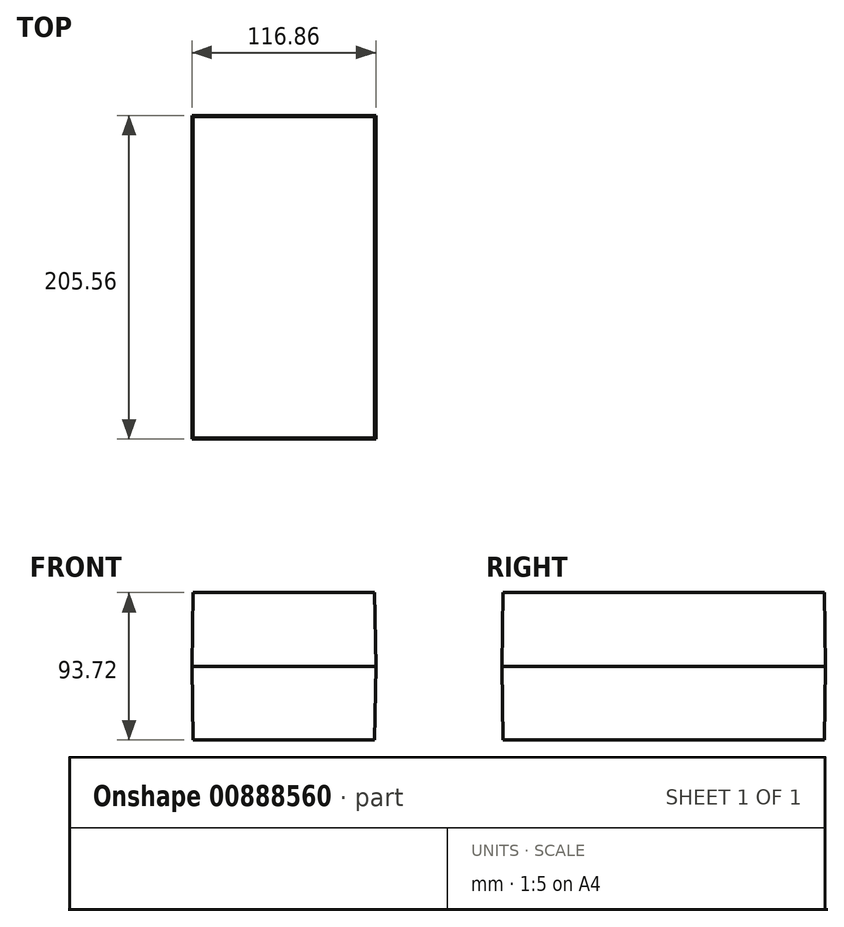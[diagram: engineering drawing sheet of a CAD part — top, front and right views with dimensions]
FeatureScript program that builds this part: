
annotation { "Feature Type Name" : "Feature", "Feature Type Description" : "" }
export const myFeature = defineFeature(function(context is Context, id is Id, definition is map)
    precondition{}
    {
        {
            var Q0;
            Q0=qCreatedBy(makeId("Top.planeOp"),FACE);
            var sketch = newSketch(context, id + "F0", { "sketchPlane" : qUnion([Q0])});
            skLineSegment(sketch, "E0.bottom", {"start": v(-103.11, 32.39) * mm, "end": v(13.75, 32.39) * mm});
            skLineSegment(sketch, "E0.top", {"start": v(-103.11, -173.17) * mm, "end": v(13.75, -173.17) * mm});
            skLineSegment(sketch, "E0.left", {"start": v(-103.11, 32.39) * mm, "end": v(-103.11, -173.17) * mm});
            skLineSegment(sketch, "E0.right", {"start": v(13.75, 32.39) * mm, "end": v(13.75, -173.17) * mm});
            skSolve(sketch);
        }
        {
            var Q0;
            Q0=makeQuery(id+"F0.imprint","IMPRINT",FACE,{"disambiguationData":[TD([[makeQuery(id+"F0.imprint","IMPRINT",EDGE,{"derivedFrom":sQuery(id+"F0.wireOp",EDGE,"E0.bottom")}),-1.0]])]});
            var Q1;
            Q1=sQuery(id+"F0.wireOp",EDGE,"E0.left");
            var Q2;
            Q2=sQuery(id+"F0.wireOp",EDGE,"E0.bottom");
            var Q3;
            Q3=sQuery(id+"F0.wireOp",EDGE,"E0.right");
            var Q4;
            Q4=sQuery(id+"F0.wireOp",EDGE,"E0.top");
            extrude(context, id + "F1", {"entities" : qUnion([Q0]), "surfaceEntities" : qUnion([Q1, Q2, Q3, Q4]), "endBound" : BoundingType.SYMMETRIC, "depth" : 93.73 * mm, "offsetDistance" : 25.4 * mm, "hasDraft" : true, "draftAngle" : 1 * degree, "draftPullDirection" : true});
        }
    });
